# Revit family: Hager-Univers-IP41-D400-H1850-Cl.I-Steel_encl-PL-pl
name_source: partatom
category: Equipement électrique
units: mm (PartAtom-declared; Revit-internal decimal feet)

## family parameters
Configuration du panneau = Deux colonnes, circuits au sein
Cote de connecteur circulaire = Utiliser le diamètre
Couper avec des vides une fois chargée = Non
Hôte = Face
Partagée = Non
Point de calcul de pièce = Non
Type d'élément = Tableau de raccordement

## types (5) — shared parameters
Commentaires du type = Univers
EF000003 - Sposób montażu = EV000384 - Montaż natynkowy
EF000007 - Kolor = EV000270 - Szary
EF000040 - Wysokość = 1850 mm  [stored 6.06955 ft]
EF000049 - Głębokość = 400 mm  [stored 1.31234 ft]
EF000116 - Numer RAL = 7035
EF000118 - Z płytą montażową = Non
EF000266 - Liczba rzędów = 12
EF000339 - Rodzaj pokrywy = EV004216 - Drzwi
EF001088 - Możliwość rozbudowy = Oui
EF001131 - Głębokość wewnętrzna = 400 mm  [stored 1.31234 ft]
EF001596 - Materiał obudowy = EV000179 - Stal
EF001613 - Podtrzymanie funkcji = EV000494 - Brak
EF002950 - Szerokość wyrażona liczbą modułów = 24
EF003532 - Do zastosowań zewnętrznych = Non
EF004293 - Odporność udarowa = EV006813 - IK07
EF005474 - Stopień ochrony (IP) = EV006416 - IP41
EF006244 - Transparentna pokrywa/drzwi = Non
EF006306 - Z zamkiem = Non
EF007800 - Do ochrony odgromowej = Non
EF008873 - Prąd znamionowy (In) = 800 A
EF009170 - Obudowa z materiału o wysokiej wytrzymałości mechanicznej = 2 mm  [stored 0.00656168 ft]
EF009171 - Drzwi/pokrywa z materiału o wysokiej wytrzymałości mechanicznej = 2 mm  [stored 0.00656168 ft]
EF009212 - Wykonanie pokrywy = EV000116 - Zamknięty
EF015940 - Pokrywa z wyzwalaczem nadciśnieniowym = Non
Fabricant = Hager
HG000002 - Z drzwiami lub pokrywą = Oui
HG000003 - Zakres = Univers
HG000006 - Montaż podtynkowy = Non
HG000010 - Drzwi asymetryczne = Non
HG000023 - Obudowa dwusekcyjna = Non
HG000024 - Wysokość części dolnej = 800 mm  [stored 2.62467 ft]
HG000026 - Stojąca = Non
zero-valued in all types: EF000218 - Głębokość wbudowania, Elévation par défaut, HG000027 - Wysokość cokołu

## per-type parameters (varying)
| type | EF000008 - Szerokość | EF000437 - Liczba wejść kablowych | EF004427 - Liczba modułów | EF004464 - Rodzaj drzwi | EF009554 - Liczba otworów pod flansze | HG000004 - Referencja producenta | HG000009 - Drzwi dwuskrzydłowe |
| Montaż natynkowy IP41 S1050 W1850 G400  - FS24G | 1050 mm | 8 | 576 | EV003602 - Podwójny | 8 | FS24G | Oui |
| Montaż natynkowy IP41 S1300 W1850 G400  - FS25G | 1300 mm  [stored 4.26509 ft] | 10 | 720 | EV003602 - Podwójny | 10 | FS25G | Oui |
| Montaż natynkowy IP41 S300 W1850 G400  - FS21G | 300 mm | 2 | 144 | EV002646 - Pojedynczy | 2 | FS21G | Non |
| Montaż natynkowy IP41 S550 W1850 G400  - FS22G | 550 mm | 4 | 288 | EV002646 - Pojedynczy | 4 | FS22G | Non |
| Montaż natynkowy IP41 S800 W1850 G400  - FS23G | 800 mm  [stored 2.62467 ft] | 6 | 432 | EV002646 - Pojedynczy | 6 | FS23G | Non |

note: [stored X ft] marks values corroborated as IEEE doubles in the binary element streams (Revit-internal decimal feet)

## geometry (parser evidence)
native form markers: Sweep x10
no freeform markers — native parametric forms only
